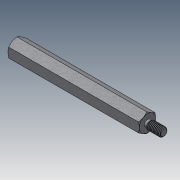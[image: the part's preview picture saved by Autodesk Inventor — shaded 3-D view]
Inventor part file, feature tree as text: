
AUTODESK INVENTOR PART (.ipt)
format: ipt  version: 2018.3 (Build 223284000, 284)  size: 578,048 bytes
history: native  units: in
note: dims shown in document units (in); Inventor stores cm internally (conversion verified against a paired STEP export)
features: extrude x1
ambient origin geometry x8: Origin, YZ Plane, XZ Plane, XY Plane, X Axis, Y Axis, Z Axis, Center Point
bodies: Solid1 (feature_tree)
feature tree (1):
  extrude  "Extrude8"  [1 undecoded]
note: 1 required parameter value undecoded (feature->parameter linkage not recoverable at this tier; creation-order binding heuristic only, values carry confidence <= 0.55)
